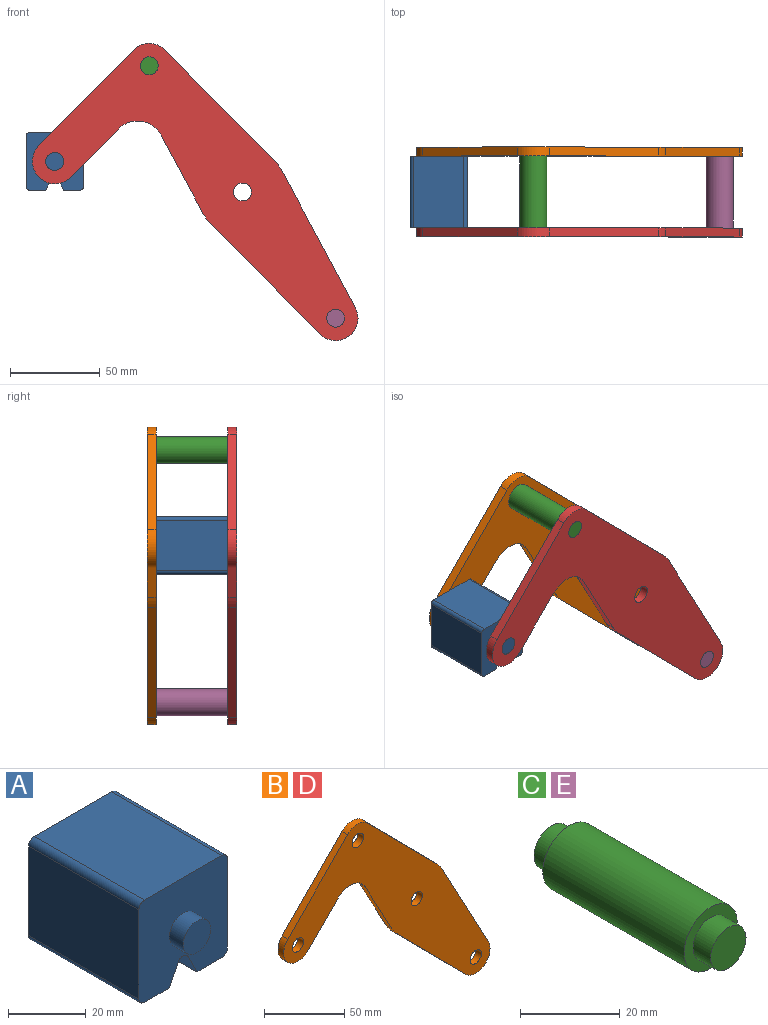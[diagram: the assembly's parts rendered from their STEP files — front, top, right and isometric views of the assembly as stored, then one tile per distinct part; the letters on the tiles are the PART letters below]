
ASSEMBLY  parts=5 mates=3
PART A: 18 faces, bbox 32.1x50x32.1 mm
  f0: plane 40x28.08mm, normal (1,0,0), area 1123.1mm2, adj f4,f10,f13,f14
  f1: plane 40x9.04mm, normal (0,0,-1), area 361.6mm2, adj f2,f4,f10,f14
  f2: plane 40x6.42mm, normal (-0.89,0,-0.45), area 287.2mm2, adj f1,f4,f10,f15
  f3: plane 40x6.42mm, normal (0.89,0,-0.45), area 287.2mm2, adj f4,f5,f10,f15
  f4: plane 32.08x32.08mm, normal (0,-1,0), area 900.6mm2, adj f0,f1,f2,f3,f5,f6,f7,f9
  f5: plane 40x9.04mm, normal (0,0,-1), area 361.6mm2, adj f3,f4,f10,f16
  f6: plane 40x28.08mm, normal (0,0,1), area 1123.1mm2, adj f4,f10,f13,f17
  f7: plane 40x28.08mm, normal (-1,0,0), area 1123.1mm2, adj f4,f10,f16,f17
  f8: plane 10x10mm, normal (0,-1,0), area 78.5mm2, adj f9
  f9: cylinder r=5mm len=10mm, axis (0,1,0), area 157.1mm2, adj f4,f8
  f10: plane 32.08x32.08mm, normal (0,1,0), area 900.6mm2, adj f0,f1,f2,f3,f5,f6,f7,f12
  f11: plane 10x10mm, normal (0,1,0), area 78.5mm2, adj f12
  f12: cylinder r=5mm len=10mm, axis (0,-1,0), area 157.1mm2, adj f10,f11
  f13: cylinder r=2mm len=40mm, axis (0,1,0), area 125.7mm2, adj f0,f4,f6,f10
  f14: cylinder r=2mm len=40mm, axis (0,-1,0), area 125.7mm2, adj f0,f1,f4,f10
  f15: cylinder r=2mm len=40mm, axis (0,1,0), area 177.1mm2, adj f2,f3,f4,f10
  f16: cylinder r=2mm len=40mm, axis (0,1,0), area 125.7mm2, adj f4,f5,f7,f10
  f17: cylinder r=2mm len=40mm, axis (0,-1,0), area 125.7mm2, adj f4,f6,f7,f10
PART B: 18 faces, bbox 181.7x5x165.8 mm
  f0: plane 43.49x23.35mm, normal (-0.88,0,-0.47), area 246.8mm2, adj f1,f14,f16,f17
  f1: cylinder r=25mm len=5.75mm, axis (0,1,0), area 35.8mm2, adj f0,f2,f16,f17
  f2: plane 61.6x60.87mm, normal (-0.71,0,-0.7), area 433mm2, adj f1,f3,f16,f17
  f3: cylinder r=12.5mm len=21.39mm, axis (0,1,0), area 178.4mm2, adj f2,f4,f16,f17
  f4: plane 76.3x40.96mm, normal (0.88,0,0.47), area 433mm2, adj f3,f5,f16,f17
  f5: cylinder r=25mm len=5.75mm, axis (0,1,0), area 35.8mm2, adj f4,f6,f16,f17
  f6: plane 61.6x60.87mm, normal (0.71,0,0.7), area 433mm2, adj f5,f7,f16,f17
  f7: cylinder r=12.5mm len=17.78mm, axis (0,1,0), area 98.9mm2, adj f6,f8,f16,f17
  f8: plane 53.35x52.71mm, normal (-0.71,0,0.7), area 375mm2, adj f7,f9,f16,f17
  f9: cylinder r=12.5mm len=21.39mm, axis (0,1,0), area 196.3mm2, adj f8,f10,f16,f17
  f10: plane 26.86x26.54mm, normal (0.71,0,-0.7), area 188.8mm2, adj f9,f14,f16,f17
  f11: cylinder r=5mm len=10mm, axis (0,1,0), area 157.1mm2, adj f16,f17
  f12: cylinder r=5mm len=10mm, axis (0,1,0), area 157.1mm2, adj f16,f17
  f13: cylinder r=5mm len=10mm, axis (0,1,0), area 157.1mm2, adj f16,f17
  f14: cylinder r=15mm len=23.89mm, axis (0,1,0), area 140.2mm2, adj f0,f10,f16,f17
  f15: cylinder r=5mm len=10mm, axis (0,1,0), area 157.1mm2, adj f16,f17
  f16: plane 181.66x165.78mm, normal (0,-1,0), area 8710.1mm2, adj f0,f1,f2,f3,f4,f5,f6,f7
  f17: plane 181.66x165.78mm, normal (0,1,0), area 8710.1mm2, adj f0,f1,f2,f3,f4,f5,f6,f7
PART C: 7 faces, bbox 15x50x15 mm
  f0: cylinder r=7.5mm len=40mm, axis (0,-1,0), area 1885mm2, adj f2,f5
  f1: cylinder r=5mm len=10mm, axis (0,1,0), area 157.1mm2, adj f2,f3
  f2: plane 15x15mm, normal (0,-1,0), area 98.2mm2, adj f0,f1
  f3: plane 10x10mm, normal (0,-1,0), area 78.5mm2, adj f1
  f4: cylinder r=5mm len=10mm, axis (0,-1,0), area 157.1mm2, adj f5,f6
  f5: plane 15x15mm, normal (0,1,0), area 98.2mm2, adj f0,f4
  f6: plane 10x10mm, normal (0,1,0), area 78.5mm2, adj f4
PART D: same geometry as B
PART E: same geometry as C
PLACE A t=(0,-20,0)mm
PLACE B t=(0,25,0)mm
PLACE C t=(0,-20,0)mm
PLACE D t=(0,-20,0)mm fixed
PLACE E t=(103.95,-20,-140.78)mm
MATE fastened E.f0 <-> D.f3  axis (0,-1,0) through (51.98,-20,-70.39)mm
MATE fastened B.f7 <-> C.f0  axis (0,-1,0) through (-51.98,20,70.39)mm
MATE revolute A.f9 <-> D.f9  axis (0,-1,0) through (-104.69,-20,17.04)mm
